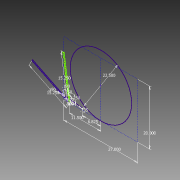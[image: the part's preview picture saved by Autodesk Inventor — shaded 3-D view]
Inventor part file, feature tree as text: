
AUTODESK INVENTOR PART (.ipt)
format: ipt  version: 2014 (Build 180170000, 170)  size: 81,920 bytes
history: native  units: in
note: dims shown in document units (in); Inventor stores cm internally (conversion verified against a paired STEP export)
features: sketch x1
ambient origin geometry x8: Origin, YZ Plane, XZ Plane, XY Plane, X Axis, Y Axis, Z Axis, Center Point
feature tree (1):
  sketch  "Sketch1"  dims[d0=22.5in d1=27.0in d2=20.0in d3=0.5in d4=15.25in d5=11.5in d7=0.19in d8=3.25in d9=7.622in d10=0.735in d12=6.825in d13=15.25in d14=0.5in d15=0.19in d16=3.25in]
